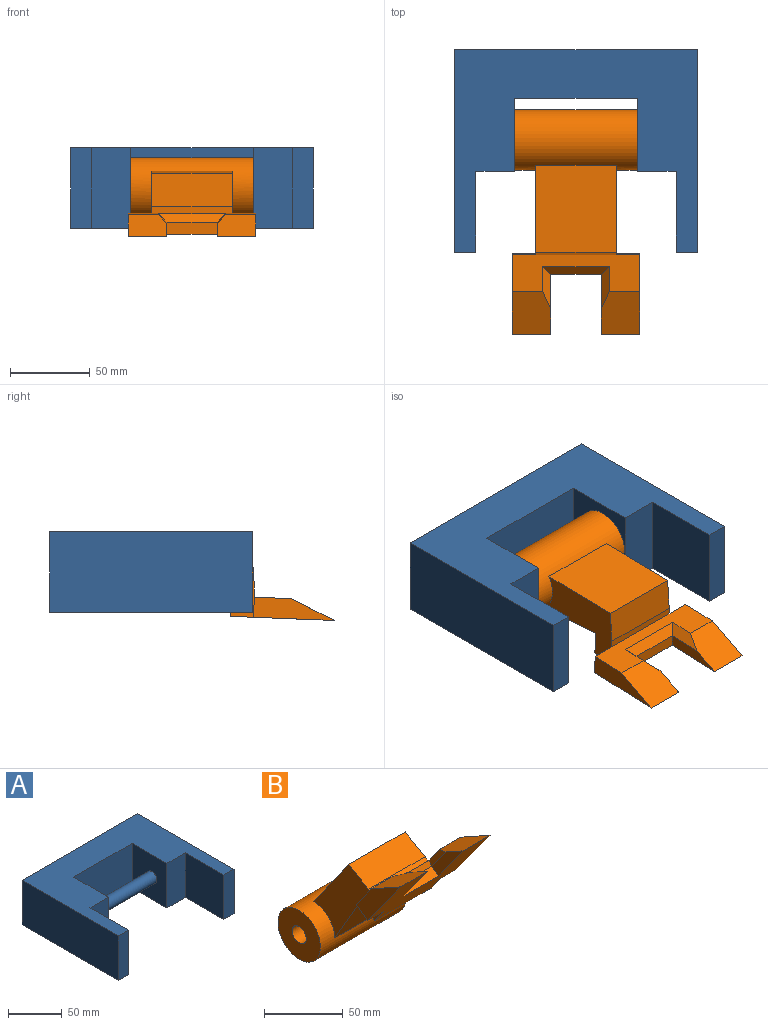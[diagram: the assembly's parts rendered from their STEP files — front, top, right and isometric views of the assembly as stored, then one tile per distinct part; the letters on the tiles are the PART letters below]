
ASSEMBLY  parts=2 mates=1
PART A: 15 faces, bbox 152.4x127x50.8 mm
  f0: plane 50.8x13.32mm, normal (0,-1,0), area 676.4mm2, adj f4,f8,f9,f14
  f1: plane 50.8x13.32mm, normal (0,-1,0), area 676.4mm2, adj f2,f8,f9,f11
  f2: plane 127x50.8mm, normal (1,0,0), area 6451.6mm2, adj f1,f3,f8,f9
  f3: plane 152.4x50.8mm, normal (0,1,0), area 7741.9mm2, adj f2,f4,f8,f9
  f4: plane 127x50.8mm, normal (-1,0,0), area 6451.6mm2, adj f0,f3,f8,f9
  f5: plane 50.8x45.86mm, normal (1,0,0), area 2203.1mm2, adj f6,f8,f9,f10,f13
  f6: plane 77x50.8mm, normal (0,-1,0), area 3911.4mm2, adj f5,f7,f8,f9
  f7: plane 50.8x45.86mm, normal (-1,0,0), area 2203.1mm2, adj f6,f8,f9,f10,f12
  f8: plane 152.4x127mm, normal (0,0,1), area 9444.2mm2, adj f0,f1,f2,f3,f4,f5,f6,f7
  f9: plane 152.4x127mm, normal (0,0,-1), area 9444.2mm2, adj f0,f1,f2,f3,f4,f5,f6,f7
  f10: cylinder r=6.35mm len=77mm, axis (-1,0,0), area 3072mm2, adj f5,f7
  f11: plane 50.8x50.72mm, normal (-1,0,0), area 2576.7mm2, adj f1,f8,f9,f12
  f12: plane 50.8x24.39mm, normal (0,-1,0), area 1238.8mm2, adj f7,f8,f9,f11
  f13: plane 50.8x24.39mm, normal (0,-1,0), area 1238.8mm2, adj f5,f8,f9,f14
  f14: plane 50.8x50.72mm, normal (1,0,0), area 2576.7mm2, adj f0,f8,f9,f13
PART B: 25 faces, bbox 80.2x111.9x103.5 mm
  f0: plane 80.25x52.71mm, normal (0,-0.81,-0.59), area 3597.7mm2, adj f9,f10,f11,f12,f13,f15,f16,f17
  f1: plane 50.8x3.63mm, normal (0,-0.59,0.81), area 227.6mm2, adj f8,f10,f11,f14
  f2: cylinder r=6.35mm len=76.99mm, axis (-1,0,0), area 3071.7mm2, adj f4,f5
  f3: cylinder r=19.05mm len=76.99mm, axis (-1,0,0), area 7729.6mm2, adj f4,f5,f6,f7,f10,f11
  f4: plane 38.1x38.1mm, normal (1,0,0), area 1013.4mm2, adj f2,f3
  f5: plane 38.1x38.1mm, normal (-1,0,0), area 1013.4mm2, adj f2,f3
  f6: plane 50.8x40.26mm, normal (0,-0.87,-0.5), area 2355.3mm2, adj f3,f9,f10,f11
  f7: plane 50.8x44.73mm, normal (0,0.82,0.57), area 2770.3mm2, adj f3,f8,f10,f11
  f8: plane 50.8x17.98mm, normal (0,-0.5,0.87), area 1051.9mm2, adj f1,f7,f10,f11
  f9: plane 50.8x12.57mm, normal (0,0.59,-0.81), area 788.8mm2, adj f0,f6,f10,f11
  f10: plane 63.17x63.02mm, normal (1,0,0), area 1481.4mm2, adj f0,f1,f3,f6,f7,f8,f9,f16
  f11: plane 63.17x63.02mm, normal (-1,0,0), area 1481.4mm2, adj f0,f1,f3,f6,f7,f8,f9,f12
  f12: plane 14.72x10.22mm, normal (0,0.59,-0.81), area 185.8mm2, adj f0,f11,f14,f15
  f13: plane 40.99x39.93mm, normal (1,0,0), area 468.1mm2, adj f0,f14,f16,f20
  f14: plane 80.25x19.08mm, normal (0,0.81,0.59), area 1228.3mm2, adj f1,f12,f13,f15,f16,f20,f21,f22
  f15: plane 40.99x39.93mm, normal (-1,0,0), area 468.1mm2, adj f0,f12,f14,f21
  f16: plane 14.72x10.22mm, normal (0,0.59,-0.81), area 185.8mm2, adj f0,f10,f13,f14
  f17: plane 31.75x6.1mm, normal (0,-0.59,0.81), area 239.4mm2, adj f0,f18,f19,f24
  f18: plane 30.6x28.28mm, normal (-1,0,0), area 224mm2, adj f0,f17,f20,f23
  f19: plane 30.6x28.28mm, normal (1,0,0), area 224mm2, adj f0,f17,f21,f22
  f20: plane 26.1x24.25mm, normal (0,0.49,0.87), area 693.5mm2, adj f0,f13,f14,f18,f23
  f21: plane 26.1x24.25mm, normal (0,0.49,0.87), area 693.5mm2, adj f0,f14,f15,f19,f22
  f22: plane 19.79x18.64mm, normal (0.71,0.57,0.41), area 134.5mm2, adj f14,f19,f21,f24
  f23: plane 19.79x18.64mm, normal (-0.71,0.57,0.41), area 134.5mm2, adj f14,f18,f20,f24
  f24: plane 41.91x7.09mm, normal (0,0.16,0.99), area 264.6mm2, adj f14,f17,f22,f23
PLACE A t=(39.93,28.15,-17.76)mm fixed
PLACE B rot(axis=(1,0,0),56.3deg) t=(39.93,35.01,7.64)mm
MATE revolute B.f3 <-> A.f10  axis (-1,0,0) through (39.93,35.01,7.64)mm
